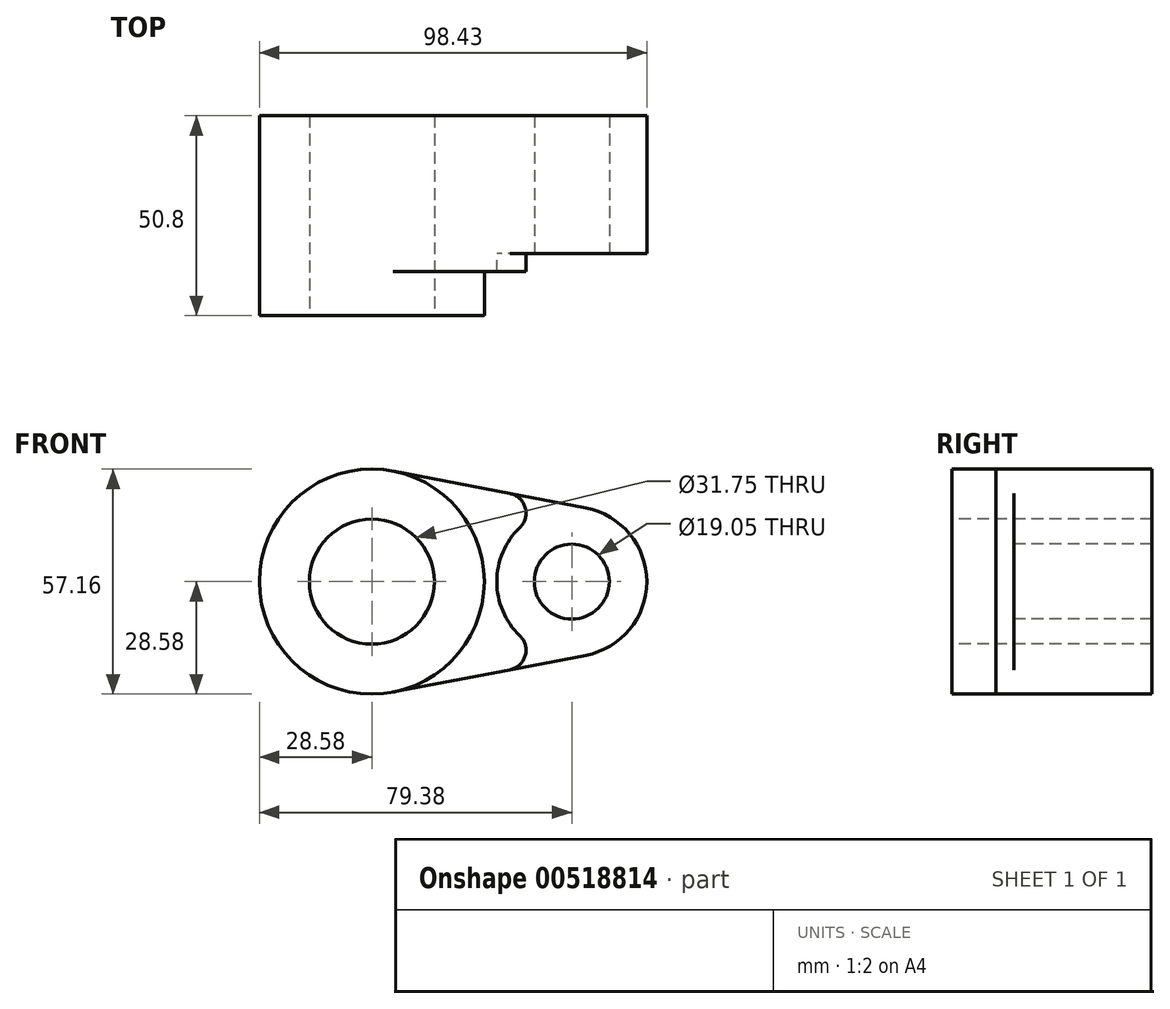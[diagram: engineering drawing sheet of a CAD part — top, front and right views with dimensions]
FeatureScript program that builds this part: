
annotation { "Feature Type Name" : "Feature", "Feature Type Description" : "" }
export const myFeature = defineFeature(function(context is Context, id is Id, definition is map)
    precondition{}
    {
        {
            var Q0;
            Q0=qCreatedBy(makeId("Front.planeOp"),FACE);
            var sketch = newSketch(context, id + "F0", { "sketchPlane" : qUnion([Q0])});
            skCircle(sketch, "E0", {"center": v(0, 0) * mm, "radius": 28.58 * mm});
            skCircle(sketch, "E1", {"center": v(50.8, 0) * mm, "radius": 19.05 * mm});
            skLineSegment(sketch, "E2", {"start": v(5.36, 28.07) * mm, "end": v(54.37, 18.71) * mm});
            skLineSegment(sketch, "E3", {"start": v(5.36, -28.07) * mm, "end": v(54.37, -18.71) * mm});
            skCircle(sketch, "E4", {"center": v(0, 0) * mm, "radius": 15.88 * mm});
            skCircle(sketch, "E5", {"center": v(50.8, 0) * mm, "radius": 9.53 * mm});
            skSolve(sketch);
        }
        {
            var Q0;
            Q0=makeQuery(id+"F0.imprint","IMPRINT",FACE,{"disambiguationData":[TD([[makeQuery(id+"F0.imprint","IMPRINT",EDGE,{"derivedFrom":sQuery(id+"F0.wireOp",EDGE,"E4")}),-1.0]])]});
            var Q1;
            {var subQ0=sQuery(id+"F0.wireOp",EDGE,"E2");Q1=makeQuery(id+"F0.imprint","IMPRINT",FACE,{"disambiguationData":[TD([[makeQuery(id+"F0.imprint","IMPRINT",EDGE,{"derivedFrom":subQ0}),-1.0]])]});}
            var Q2;
            Q2=makeQuery(id+"F0.imprint","IMPRINT",FACE,{"disambiguationData":[TD([[makeQuery(id+"F0.imprint","IMPRINT",EDGE,{"derivedFrom":sQuery(id+"F0.wireOp",EDGE,"E5")}),-1.0]])]});
            extrude(context, id + "F1", {"entities" : qUnion([Q0, Q1, Q2]), "oppositeDirection" : true, "depth" : 25.4 * mm, "offsetDistance" : 25.4 * mm});
        }
        {
            var Q0;
            Q0=makeQuery(id+"F0.imprint","IMPRINT",FACE,{"disambiguationData":[TD([[makeQuery(id+"F0.imprint","IMPRINT",EDGE,{"derivedFrom":sQuery(id+"F0.wireOp",EDGE,"E4")}),-1.0]])]});
            extrude(context, id + "F2", {"entities" : qUnion([Q0]), "operationType" : NewBodyOperationType.ADD, "depth" : 25.4 * mm, "offsetDistance" : 25.4 * mm});
        }
        {
            var Q0;
            {var subQ0=sQuery(id+"F0.wireOp",EDGE,"E2");Q0=makeQuery(id+"F0.imprint","IMPRINT",FACE,{"disambiguationData":[TD([[makeQuery(id+"F0.imprint","IMPRINT",EDGE,{"derivedFrom":subQ0}),-1.0]])]});}
            extrude(context, id + "F3", {"entities" : qUnion([Q0]), "operationType" : NewBodyOperationType.ADD, "depth" : 14.22 * mm, "offsetDistance" : 25.4 * mm});
        }
        {
            var Q0;
            Q0=makeQuery(id+"F0.imprint","IMPRINT",FACE,{"disambiguationData":[TD([[makeQuery(id+"F0.imprint","IMPRINT",EDGE,{"derivedFrom":sQuery(id+"F0.wireOp",EDGE,"E5")}),-1.0]])]});
            extrude(context, id + "F4", {"entities" : qUnion([Q0]), "operationType" : NewBodyOperationType.ADD, "depth" : 9.65 * mm, "offsetDistance" : 25.4 * mm});
        }
        {
            var Q0;
            Q0=makeQuery(id+"F4.boolean.opBoolean","SPLIT",EDGE,{"derivedFrom":makeQuery(id+"F3.opExtrude","SWEPT_EDGE",EDGE,{"disambiguationData":[OSD([sQuery(id+"F0.wireOp",EDGE,"E1"),sQuery(id+"F0.wireOp",EDGE,"E2")])]})});
            var Q1;
            Q1=makeQuery(id+"F4.boolean.opBoolean","SPLIT",EDGE,{"derivedFrom":makeQuery(id+"F3.opExtrude","SWEPT_EDGE",EDGE,{"disambiguationData":[OSD([sQuery(id+"F0.wireOp",EDGE,"E1"),sQuery(id+"F0.wireOp",EDGE,"E3")])]})});
            fillet(context, id + "F5", {"entities" : qUnion([Q0, Q1]), "radius" : 5.08 * mm, "tangentPropagation" : true, "allowEdgeOverflow" : false});
        }
    });
